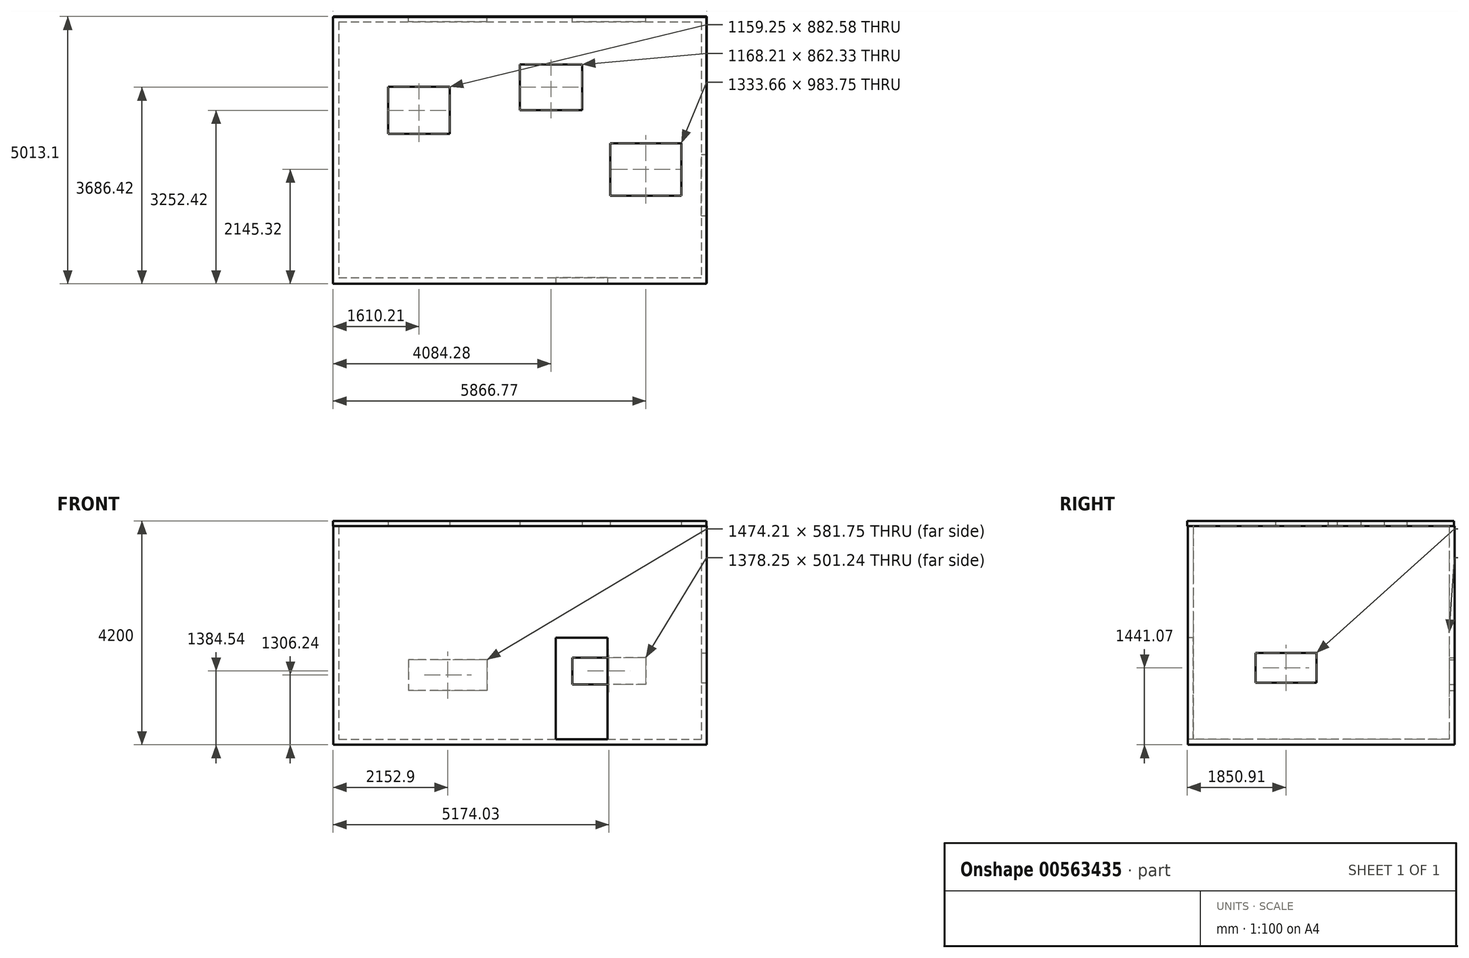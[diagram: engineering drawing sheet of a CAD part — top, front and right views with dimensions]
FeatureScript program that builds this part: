
annotation { "Feature Type Name" : "Feature", "Feature Type Description" : "" }
export const myFeature = defineFeature(function(context is Context, id is Id, definition is map)
    precondition{}
    {
        {
            var Q0;
            Q0=qCreatedBy(makeId("Top.planeOp"),FACE);
            var sketch = newSketch(context, id + "F0", { "sketchPlane" : qUnion([Q0])});
            skLineSegment(sketch, "E0.bottom", {"start": v(-3494.68, 2786.29) * mm, "end": v(3505.32, 2786.29) * mm});
            skLineSegment(sketch, "E0.top", {"start": v(-3494.68, -2213.71) * mm, "end": v(3505.32, -2213.71) * mm});
            skLineSegment(sketch, "E0.left", {"start": v(-3494.68, 2786.29) * mm, "end": v(-3494.68, -2213.71) * mm});
            skLineSegment(sketch, "E0.right", {"start": v(3505.32, 2786.29) * mm, "end": v(3505.32, -2213.71) * mm});
            skSolve(sketch);
        }
        {
            var Q0;
            Q0 = qSketchRegion(id + "F0", true);
            extrude(context, id + "F1", {"entities" : qUnion([Q0]), "depth" : 4100 * mm, "offsetDistance" : 25.4 * mm});
        }
        {
            var Q0;
            Q0=makeQuery(id+"F1.opExtrude","CAP_FACE",FACE,{"disambiguationData":[OSD([sQuery(id+"F0.wireOp",EDGE,"E0.bottom"),sQuery(id+"F0.wireOp",EDGE,"E0.top"),sQuery(id+"F0.wireOp",EDGE,"E0.left"),sQuery(id+"F0.wireOp",EDGE,"E0.right")])],"isStart":false});
            shell(context, id + "F2", {"entities" : qUnion([Q0]), "thickness" : 100 * mm});
        }
        {
            var Q0;
            Q0=makeQuery(id+"F1.opExtrude","CAP_VERTEX",VERTEX,{"disambiguationData":[OSD([sQuery(id+"F0.wireOp",EDGE,"E0.bottom"),sQuery(id+"F0.wireOp",EDGE,"E0.left")])],"isStart":false});
            var Q1;
            Q1=makeQuery(id+"F1.opExtrude","CAP_VERTEX",VERTEX,{"disambiguationData":[OSD([sQuery(id+"F0.wireOp",EDGE,"E0.bottom"),sQuery(id+"F0.wireOp",EDGE,"E0.right")])],"isStart":false});
            var Q2;
            Q2=makeQuery(id+"F1.opExtrude","CAP_VERTEX",VERTEX,{"disambiguationData":[OSD([sQuery(id+"F0.wireOp",EDGE,"E0.top"),sQuery(id+"F0.wireOp",EDGE,"E0.left")])],"isStart":false});
            cPlane(context, id + "F3", {"entities" : qUnion([Q0, Q1, Q2]), "cplaneType" : CPlaneType.THREE_POINT, "offset" : 25.4 * mm, "width" : 152.4 * mm, "height" : 152.4 * mm});
        }
        {
            var Q0;
            Q0=qCreatedBy(id+"F3.planeOp",FACE);
            var sketch = newSketch(context, id + "F4", { "sketchPlane" : qUnion([Q0])});
            skLineSegment(sketch, "E1.bottom", {"start": v(3501.6, 2774.45) * mm, "end": v(-3500.17, 2774.45) * mm});
            skLineSegment(sketch, "E1.top", {"start": v(3501.6, -2226.81) * mm, "end": v(-3500.17, -2226.81) * mm});
            skLineSegment(sketch, "E1.left", {"start": v(3501.6, 2774.45) * mm, "end": v(3501.6, -2226.81) * mm});
            skLineSegment(sketch, "E1.right", {"start": v(-3500.17, 2774.45) * mm, "end": v(-3500.17, -2226.81) * mm});
            skSolve(sketch);
        }
        {
            var Q0;
            Q0 = qSketchRegion(id + "F4", true);
            extrude(context, id + "F5", {"entities" : qUnion([Q0]), "operationType" : NewBodyOperationType.ADD, "depth" : 100 * mm, "offsetDistance" : 25.4 * mm});
        }
        {
            var Q0;
            Q0=qCreatedBy(id+"F3.planeOp",FACE);
            var sketch = newSketch(context, id + "F6", { "sketchPlane" : qUnion([Q0])});
            skLineSegment(sketch, "E2.bottom", {"start": v(-1310.33, 1466.9) * mm, "end": v(-2469.58, 1466.9) * mm});
            skLineSegment(sketch, "E2.top", {"start": v(-1310.33, 584.32) * mm, "end": v(-2469.58, 584.32) * mm});
            skLineSegment(sketch, "E2.left", {"start": v(-1310.33, 1466.9) * mm, "end": v(-1310.33, 584.32) * mm});
            skLineSegment(sketch, "E2.right", {"start": v(-2469.58, 1466.9) * mm, "end": v(-2469.58, 584.32) * mm});
            skLineSegment(sketch, "E3.bottom", {"start": v(1168.21, 1890.78) * mm, "end": v(0, 1890.78) * mm});
            skLineSegment(sketch, "E3.top", {"start": v(1168.21, 1028.45) * mm, "end": v(0, 1028.45) * mm});
            skLineSegment(sketch, "E3.left", {"start": v(1168.21, 1890.78) * mm, "end": v(1168.21, 1028.45) * mm});
            skLineSegment(sketch, "E3.right", {"start": v(0, 1890.78) * mm, "end": v(0, 1028.45) * mm});
            skLineSegment(sketch, "E4.bottom", {"start": v(3033.42, 410.39) * mm, "end": v(1699.76, 410.39) * mm});
            skLineSegment(sketch, "E4.top", {"start": v(3033.42, -573.36) * mm, "end": v(1699.76, -573.36) * mm});
            skLineSegment(sketch, "E4.left", {"start": v(3033.42, 410.39) * mm, "end": v(3033.42, -573.36) * mm});
            skLineSegment(sketch, "E4.right", {"start": v(1699.76, 410.39) * mm, "end": v(1699.76, -573.36) * mm});
            skSolve(sketch);
        }
        {
            var Q0;
            Q0 = qSketchRegion(id + "F6", true);
            extrude(context, id + "F7", {"entities" : qUnion([Q0]), "operationType" : NewBodyOperationType.REMOVE, "depth" : 150 * mm, "offsetDistance" : 25.4 * mm});
        }
        {
            var Q0;
            Q0=makeQuery(id+"F1.opExtrude","SWEPT_FACE",FACE,{"disambiguationData":[OSD([sQuery(id+"F0.wireOp",EDGE,"E0.right")])]});
            var sketch = newSketch(context, id + "F8", { "sketchPlane" : qUnion([Q0])});
            skLineSegment(sketch, "E5.bottom", {"start": v(-947.88, 1721.58) * mm, "end": v(196.08, 1721.58) * mm});
            skLineSegment(sketch, "E5.top", {"start": v(-947.88, 1160.56) * mm, "end": v(196.08, 1160.56) * mm});
            skLineSegment(sketch, "E5.left", {"start": v(-947.88, 1721.58) * mm, "end": v(-947.88, 1160.56) * mm});
            skLineSegment(sketch, "E5.right", {"start": v(196.08, 1721.58) * mm, "end": v(196.08, 1160.56) * mm});
            skSolve(sketch);
        }
        {
            var Q0;
            Q0=makeQuery(id+"F8.imprint","IMPRINT",FACE,{"disambiguationData":[TD([[makeQuery(id+"F8.imprint","IMPRINT",EDGE,{"derivedFrom":sQuery(id+"F8.wireOp",EDGE,"E5.bottom")}),-1.0]])]});
            extrude(context, id + "F9", {"entities" : qUnion([Q0]), "operationType" : NewBodyOperationType.REMOVE, "oppositeDirection" : true, "depth" : 150 * mm, "offsetDistance" : 25.4 * mm});
        }
        {
            var Q0;
            Q0=makeQuery(id+"F1.opExtrude","SWEPT_FACE",FACE,{"disambiguationData":[OSD([sQuery(id+"F0.wireOp",EDGE,"E0.bottom")])]});
            var sketch = newSketch(context, id + "F10", { "sketchPlane" : qUnion([Q0])});
            skLineSegment(sketch, "E6.bottom", {"start": v(-2362.98, 1635.16) * mm, "end": v(-984.74, 1635.16) * mm});
            skLineSegment(sketch, "E6.top", {"start": v(-2362.98, 1133.92) * mm, "end": v(-984.74, 1133.92) * mm});
            skLineSegment(sketch, "E6.left", {"start": v(-2362.98, 1635.16) * mm, "end": v(-2362.98, 1133.92) * mm});
            skLineSegment(sketch, "E6.right", {"start": v(-984.74, 1635.16) * mm, "end": v(-984.74, 1133.92) * mm});
            skLineSegment(sketch, "E7.bottom", {"start": v(610.16, 1597.12) * mm, "end": v(2084.38, 1597.12) * mm});
            skLineSegment(sketch, "E7.top", {"start": v(610.16, 1015.37) * mm, "end": v(2084.38, 1015.37) * mm});
            skLineSegment(sketch, "E7.left", {"start": v(610.16, 1597.12) * mm, "end": v(610.16, 1015.37) * mm});
            skLineSegment(sketch, "E7.right", {"start": v(2084.38, 1597.12) * mm, "end": v(2084.38, 1015.37) * mm});
            skSolve(sketch);
        }
        {
            var Q0;
            Q0 = qSketchRegion(id + "F10", true);
            extrude(context, id + "F11", {"entities" : qUnion([Q0]), "operationType" : NewBodyOperationType.REMOVE, "oppositeDirection" : true, "depth" : 150 * mm, "offsetDistance" : 25.4 * mm});
        }
        {
            var Q0;
            Q0=makeQuery(id+"F1.opExtrude","SWEPT_FACE",FACE,{"disambiguationData":[OSD([sQuery(id+"F0.wireOp",EDGE,"E0.top")])]});
            var sketch = newSketch(context, id + "F12", { "sketchPlane" : qUnion([Q0])});
            skLineSegment(sketch, "E8.bottom", {"start": v(675.87, 2005.91) * mm, "end": v(1650.5, 2005.91) * mm});
            skLineSegment(sketch, "E8.top", {"start": v(675.87, 100) * mm, "end": v(1650.5, 100) * mm});
            skLineSegment(sketch, "E8.left", {"start": v(675.87, 2005.91) * mm, "end": v(675.87, 100) * mm});
            skLineSegment(sketch, "E8.right", {"start": v(1650.5, 2005.91) * mm, "end": v(1650.5, 100) * mm});
            skSolve(sketch);
        }
        {
            var Q0;
            Q0 = qSketchRegion(id + "F12", true);
            extrude(context, id + "F13", {"entities" : qUnion([Q0]), "operationType" : NewBodyOperationType.REMOVE, "oppositeDirection" : true, "depth" : 150 * mm, "offsetDistance" : 25.4 * mm});
        }
    });
